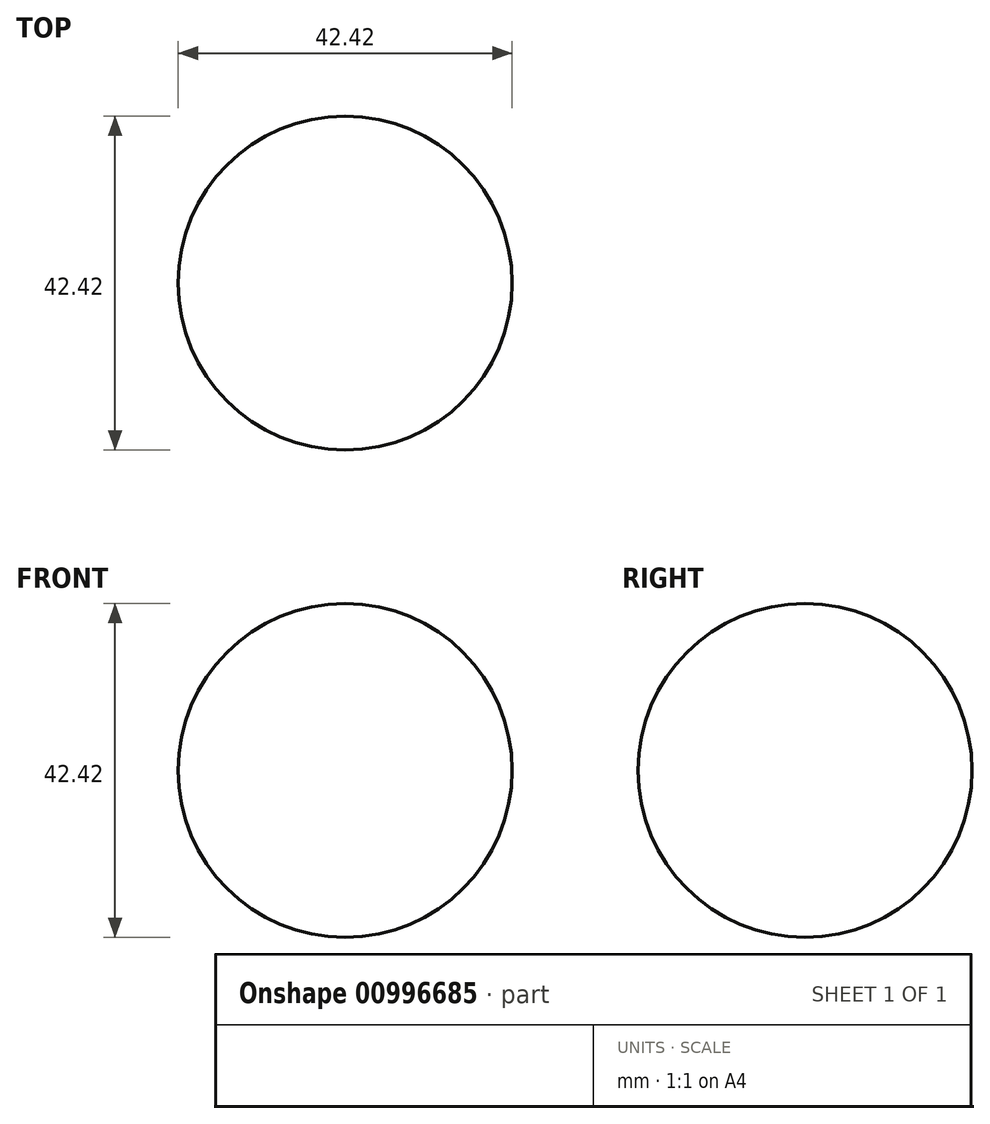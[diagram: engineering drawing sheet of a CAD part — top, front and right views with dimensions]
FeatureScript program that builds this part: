
annotation { "Feature Type Name" : "Feature", "Feature Type Description" : "" }
export const myFeature = defineFeature(function(context is Context, id is Id, definition is map)
    precondition{}
    {
        {
            var Q0;
            Q0=qCreatedBy(makeId("Front.planeOp"),FACE);
            var sketch = newSketch(context, id + "F0", { "sketchPlane" : qUnion([Q0])});
            skArc(sketch, "E0", {"start": v(0, -21.21) * mm, "mid": v(21.21, 0) * mm, "end": v(0, 21.21) * mm});
            skLineSegment(sketch, "E1", {"start": v(0, 21.21) * mm, "end": v(0, -21.21) * mm});
            skSolve(sketch);
        }
        {
            var Q0;
            Q0=makeQuery(id+"F0.imprint","IMPRINT",FACE,{"disambiguationData":[TD([[makeQuery(id+"F0.imprint","IMPRINT",EDGE,{"derivedFrom":sQuery(id+"F0.wireOp",EDGE,"E0")}),1.0]])]});
            var Q1;
            Q1=sQuery(id+"F0.wireOp",EDGE,"E1");
            revolve(context, id + "F1", {"surfaceOperationType" : NewSurfaceOperationType.NEW, "entities" : qUnion([Q0]), "axis" : qUnion([Q1]), "revolveType" : RevolveType.FULL});
        }
    });
